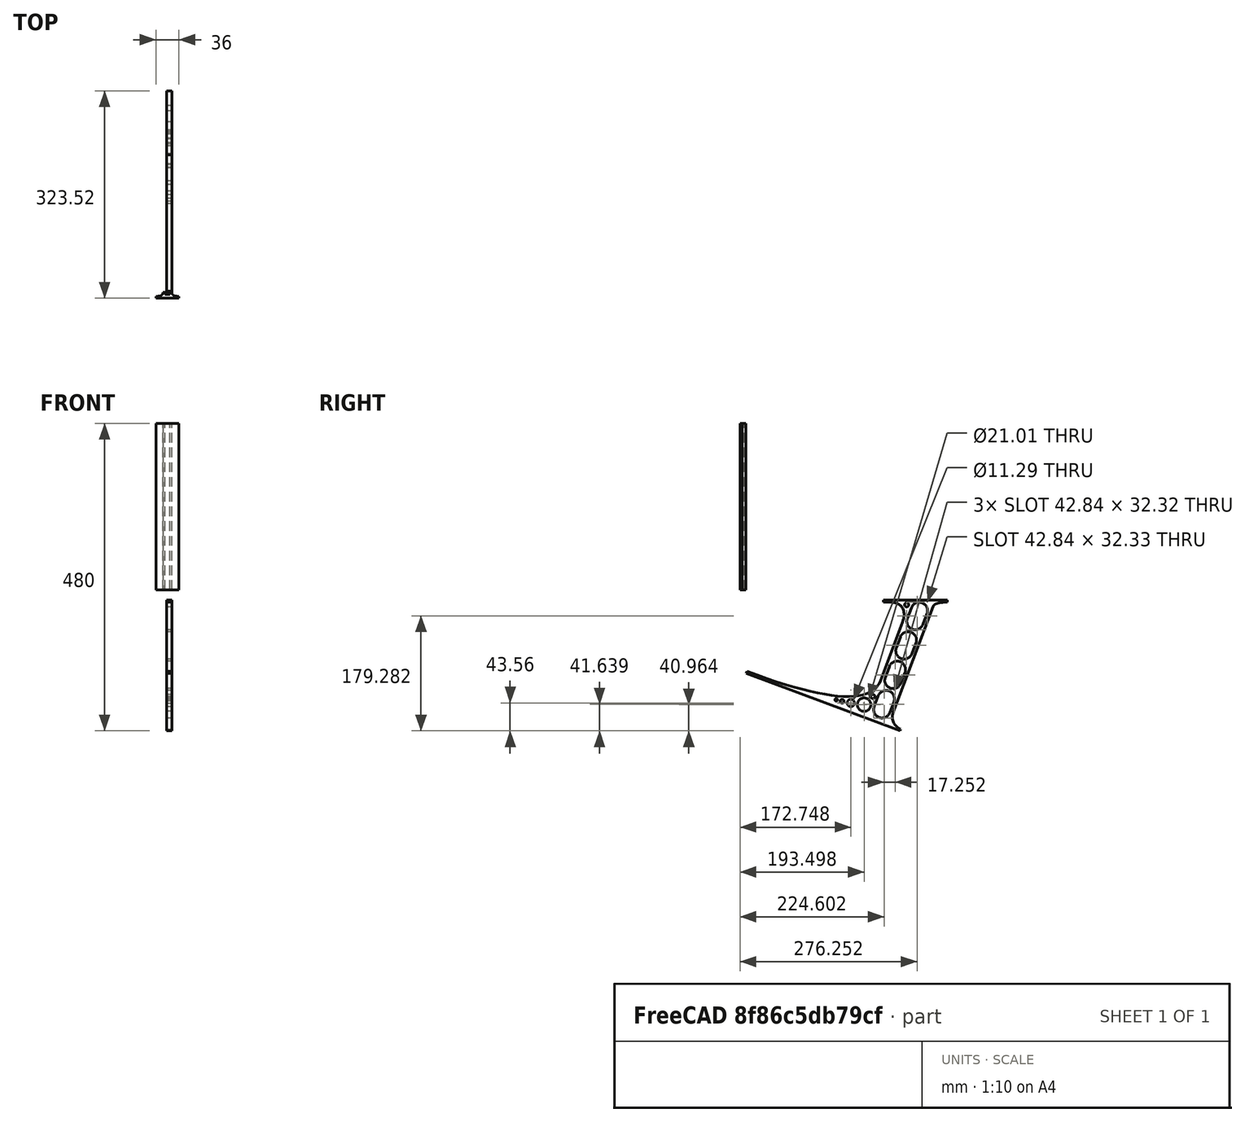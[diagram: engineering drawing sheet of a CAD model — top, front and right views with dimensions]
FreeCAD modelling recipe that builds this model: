
FCSTD DOCUMENT  (FreeCAD 0.19R0.19.2)
Label: laptopStand116FCStd
License: All rights reserved
LicenseURL: http://en.wikipedia.org/wiki/All_rights_reserved
objects: Sketcher::SketchObject×3, Part::Extrusion×3
note: 6 computed .brp shape members not serialized (recipe doc carries the construction recipe); baked Part::Feature solids carry a one-line shape summary decoded from their .brp

FEATURE [Sketcher::SketchObject] Sketch
  FullyConstrained = true
  sketch-geometry (342):
    g0: LineSegment StartX=-10.9272 StartY=-82.7794 StartZ=0 EndX=46.0728 EndY=-51.4823 EndZ=0
    g1: LineSegment StartX=-10.9272 StartY=77.3346 StartZ=0 EndX=-10.9272 EndY=-82.7794 EndZ=0
    g2: LineSegment StartX=-1.92719 StartY=-91.7794 StartZ=0 EndX=46.0728 EndY=-91.7794 EndZ=0
    g3: LineSegment StartX=46.0728 StartY=-65.424 StartZ=0 EndX=-1.92719 EndY=-91.7794 EndZ=0
    g4: LineSegment StartX=46.0728 StartY=-65.424 StartZ=0 EndX=46.0728 EndY=-91.7794 EndZ=0
    g5: LineSegment StartX=46.0728 StartY=77.3346 StartZ=0 EndX=46.0728 EndY=-51.4823 EndZ=0
    g6: LineSegment StartX=-42.9272 StartY=136.221 StartZ=0 EndX=-42.9272 EndY=-103.779 EndZ=0
    g7: LineSegment StartX=407.073 StartY=136.221 StartZ=0 EndX=407.073 EndY=-103.779 EndZ=0
    g8: ArcOfCircle CenterX=-26.9272 CenterY=22.1087 CenterZ=0 NormalX=0 NormalY=0 NormalZ=1 AngleXU=0 Radius=8 StartAngle=1e-16 EndAngle=3.14159
    g9: ArcOfCircle CenterX=-26.9272 CenterY=-83.7794 CenterZ=0 NormalX=0 NormalY=0 NormalZ=1 AngleXU=0 Radius=8 StartAngle=3.14159 EndAngle=6.28319
    g10: LineSegment StartX=-34.9272 StartY=22.1087 StartZ=0 EndX=-34.9272 EndY=-83.7794 EndZ=0
    g11: LineSegment StartX=-18.9272 StartY=22.1087 StartZ=0 EndX=-18.9272 EndY=-83.7794 EndZ=0
    g12: ArcOfCircle CenterX=391.073 CenterY=22.1087 CenterZ=0 NormalX=0 NormalY=0 NormalZ=1 AngleXU=0 Radius=8 StartAngle=-4.4e-15 EndAngle=3.14159
    g13: LineSegment StartX=399.073 StartY=22.1087 StartZ=0 EndX=399.073 EndY=-83.7794 EndZ=0
    g14: LineSegment StartX=383.073 StartY=22.1087 StartZ=0 EndX=383.073 EndY=-83.7794 EndZ=0
    g15: ArcOfCircle CenterX=391.073 CenterY=-83.7794 CenterZ=0 NormalX=0 NormalY=0 NormalZ=1 AngleXU=0 Radius=8 StartAngle=3.14159 EndAngle=6.28319
    g16: Circle CenterX=175.022 CenterY=27.0628 CenterZ=0 NormalX=0 NormalY=0 NormalZ=1 AngleXU=0 Radius=1
    g17: Circle CenterX=179.022 CenterY=24.8665 CenterZ=0 NormalX=0 NormalY=0 NormalZ=1 AngleXU=0 Radius=1
    g18: Circle CenterX=179.022 CenterY=27.0628 CenterZ=0 NormalX=0 NormalY=0 NormalZ=1 AngleXU=0 Radius=1
    g19: BSplineCurve PolesCount=3 KnotsCount=2 Degree=2 IsPeriodic=0
    g20: GeomPoint X=175.022 Y=27.0628 Z=0
    g21: GeomPoint X=179.022 Y=27.0628 Z=0
    g22: Circle CenterX=189.124 CenterY=27.0628 CenterZ=0 NormalX=0 NormalY=0 NormalZ=1 AngleXU=0 Radius=1
    g23: Circle CenterX=185.124 CenterY=24.8665 CenterZ=0 NormalX=0 NormalY=0 NormalZ=1 AngleXU=0 Radius=1
    g24: Circle CenterX=185.124 CenterY=27.0628 CenterZ=0 NormalX=0 NormalY=0 NormalZ=1 AngleXU=0 Radius=1
    g25: BSplineCurve PolesCount=3 KnotsCount=2 Degree=2 IsPeriodic=0
    g26: GeomPoint X=189.124 Y=27.0628 Z=0
    g27: GeomPoint X=185.124 Y=27.0628 Z=0
    g28: Circle CenterX=175.022 CenterY=5.37834 CenterZ=0 NormalX=0 NormalY=0 NormalZ=1 AngleXU=0 Radius=1
    g29: Circle CenterX=179.022 CenterY=7.57463 CenterZ=0 NormalX=0 NormalY=0 NormalZ=1 AngleXU=0 Radius=1
    g30: Circle CenterX=179.022 CenterY=5.34704 CenterZ=0 NormalX=0 NormalY=0 NormalZ=1 AngleXU=0 Radius=1
    g31: BSplineCurve PolesCount=3 KnotsCount=2 Degree=2 IsPeriodic=0
    g32: GeomPoint X=175.022 Y=5.37834 Z=0
    g33: GeomPoint X=179.022 Y=5.34704 Z=0
    g34: Circle CenterX=189.124 CenterY=5.37834 CenterZ=0 NormalX=0 NormalY=0 NormalZ=1 AngleXU=0 Radius=1
    g35: Circle CenterX=185.124 CenterY=7.57463 CenterZ=0 NormalX=0 NormalY=0 NormalZ=1 AngleXU=0 Radius=1
    g36: Circle CenterX=185.124 CenterY=5.34704 CenterZ=0 NormalX=0 NormalY=0 NormalZ=1 AngleXU=0 Radius=1
    g37: BSplineCurve PolesCount=3 KnotsCount=2 Degree=2 IsPeriodic=0
    g38: GeomPoint X=189.124 Y=5.37834 Z=0
    g39: GeomPoint X=185.124 Y=5.34704 Z=0
    g40: Circle CenterX=165.871 CenterY=18.1458 CenterZ=0 NormalX=0 NormalY=0 NormalZ=1 AngleXU=0 Radius=1
    g41: Circle CenterX=169.377 CenterY=16.2206 CenterZ=0 NormalX=0 NormalY=0 NormalZ=1 AngleXU=0 Radius=1
    g42: Circle CenterX=165.871 CenterY=14.2954 CenterZ=0 NormalX=0 NormalY=0 NormalZ=1 AngleXU=0 Radius=1
    g43: BSplineCurve PolesCount=3 KnotsCount=2 Degree=2 IsPeriodic=0
    g44: GeomPoint X=165.871 Y=18.1458 Z=0
    g45: GeomPoint X=165.871 Y=14.2954 Z=0
    g46: Circle CenterX=198.275 CenterY=18.1458 CenterZ=0 NormalX=0 NormalY=0 NormalZ=1 AngleXU=0 Radius=1
    g47: Circle CenterX=194.768 CenterY=16.2206 CenterZ=0 NormalX=0 NormalY=0 NormalZ=1 AngleXU=0 Radius=1
    g48: Circle CenterX=198.275 CenterY=14.2954 CenterZ=0 NormalX=0 NormalY=0 NormalZ=1 AngleXU=0 Radius=1
    g49: BSplineCurve PolesCount=3 KnotsCount=2 Degree=2 IsPeriodic=0
    g50: GeomPoint X=198.275 Y=18.1458 Z=0
    g51: GeomPoint X=198.275 Y=14.2954 Z=0
    g52: LineSegment StartX=407.073 StartY=-103.779 StartZ=0 EndX=-42.9272 EndY=-103.779 EndZ=0
    g53: LineSegment StartX=407.073 StartY=136.221 StartZ=0 EndX=-42.9272 EndY=136.221 EndZ=0
    g54: LineSegment StartX=46.0728 StartY=77.3346 StartZ=0 EndX=-10.9272 EndY=77.3346 EndZ=0
    g55: LineSegment StartX=46.0728 StartY=105.865 StartZ=0 EndX=31.5028 EndY=105.865 EndZ=0
    g56: LineSegment StartX=46.0728 StartY=124.221 StartZ=0 EndX=46.0728 EndY=105.865 EndZ=0
    g57: LineSegment StartX=-1.92719 StartY=124.221 StartZ=0 EndX=31.5028 EndY=105.865 EndZ=0
    g58: LineSegment StartX=46.0728 StartY=124.221 StartZ=0 EndX=-1.92719 EndY=124.221 EndZ=0
    g59: Circle CenterX=125.607 CenterY=54.1951 CenterZ=0 NormalX=0 NormalY=0 NormalZ=1 AngleXU=0 Radius=1
    g60: Circle CenterX=139.632 CenterY=46.4944 CenterZ=0 NormalX=0 NormalY=0 NormalZ=1 AngleXU=0 Radius=1
    g61: Circle CenterX=127.326 CenterY=56.7187 CenterZ=0 NormalX=0 NormalY=0 NormalZ=1 AngleXU=0 Radius=1
    g62: BSplineCurve PolesCount=3 KnotsCount=2 Degree=2 IsPeriodic=0
    g63: GeomPoint X=125.607 Y=54.1951 Z=0
    g64: GeomPoint X=127.326 Y=56.7187 Z=0
    g65: Circle CenterX=236.821 CenterY=56.7187 CenterZ=0 NormalX=0 NormalY=0 NormalZ=1 AngleXU=0 Radius=1
    g66: Circle CenterX=224.513 CenterY=46.4944 CenterZ=0 NormalX=0 NormalY=0 NormalZ=1 AngleXU=0 Radius=1
    g67: Circle CenterX=238.538 CenterY=54.1951 CenterZ=0 NormalX=0 NormalY=0 NormalZ=1 AngleXU=0 Radius=1
    g68: BSplineCurve PolesCount=3 KnotsCount=2 Degree=2 IsPeriodic=0
    g69: GeomPoint X=236.821 Y=56.7187 Z=0
    g70: GeomPoint X=238.538 Y=54.1951 Z=0
    g71: Circle CenterX=238.538 CenterY=-21.7539 CenterZ=0 NormalX=0 NormalY=0 NormalZ=1 AngleXU=0 Radius=1
    g72: Circle CenterX=224.513 CenterY=-14.0532 CenterZ=0 NormalX=0 NormalY=0 NormalZ=1 AngleXU=0 Radius=1
    g73: Circle CenterX=236.821 CenterY=-24.2775 CenterZ=0 NormalX=0 NormalY=0 NormalZ=1 AngleXU=0 Radius=1
    g74: BSplineCurve PolesCount=3 KnotsCount=2 Degree=2 IsPeriodic=0
    g75: GeomPoint X=238.538 Y=-21.7539 Z=0
    g76: GeomPoint X=236.821 Y=-24.2775 Z=0
    g77: Circle CenterX=125.607 CenterY=-21.7539 CenterZ=0 NormalX=0 NormalY=0 NormalZ=1 AngleXU=0 Radius=1
    g78: Circle CenterX=139.632 CenterY=-14.0532 CenterZ=0 NormalX=0 NormalY=0 NormalZ=1 AngleXU=0 Radius=1
    g79: Circle CenterX=127.325 CenterY=-24.2775 CenterZ=0 NormalX=0 NormalY=0 NormalZ=1 AngleXU=0 Radius=1
    g80: BSplineCurve PolesCount=3 KnotsCount=2 Degree=2 IsPeriodic=0
    g81: GeomPoint X=125.607 Y=-21.7539 Z=0
    g82: GeomPoint X=127.325 Y=-24.2775 Z=0
    g83: Circle CenterX=302.996 CenterY=111.695 CenterZ=0 NormalX=0 NormalY=0 NormalZ=1 AngleXU=0 Radius=1
    g84: Circle CenterX=306.073 CenterY=114.251 CenterZ=0 NormalX=0 NormalY=0 NormalZ=1 AngleXU=0 Radius=1
    g85: Circle CenterX=306.073 CenterY=110.251 CenterZ=0 NormalX=0 NormalY=0 NormalZ=1 AngleXU=0 Radius=1
    g86: BSplineCurve PolesCount=3 KnotsCount=2 Degree=2 IsPeriodic=0
    g87: GeomPoint X=302.996 Y=111.695 Z=0
    g88: GeomPoint X=306.073 Y=110.251 Z=0
    g89: Circle CenterX=306.073 CenterY=95.2763 CenterZ=0 NormalX=0 NormalY=0 NormalZ=1 AngleXU=0 Radius=1
    g90: Circle CenterX=306.073 CenterY=91.2763 CenterZ=0 NormalX=0 NormalY=0 NormalZ=1 AngleXU=0 Radius=1
    g91: Circle CenterX=302.567 CenterY=89.3511 CenterZ=0 NormalX=0 NormalY=0 NormalZ=1 AngleXU=0 Radius=1
    g92: BSplineCurve PolesCount=3 KnotsCount=2 Degree=2 IsPeriodic=0
    g93: GeomPoint X=306.073 Y=95.2763 Z=0
    g94: GeomPoint X=302.567 Y=89.3511 Z=0
    g95: LineSegment StartX=306.073 StartY=110.251 StartZ=0 EndX=306.073 EndY=95.2763 EndZ=0
    g96: LineSegment StartX=302.996 StartY=111.695 StartZ=0 EndX=236.821 EndY=56.7187 EndZ=0
    g97: LineSegment StartX=238.538 StartY=54.1951 StartZ=0 EndX=302.567 EndY=89.3511 EndZ=0
    g98: Circle CenterX=61.1496 CenterY=111.695 CenterZ=0 NormalX=0 NormalY=0 NormalZ=1 AngleXU=0 Radius=1
    g99: Circle CenterX=58.0728 CenterY=114.251 CenterZ=0 NormalX=0 NormalY=0 NormalZ=1 AngleXU=0 Radius=1
    g100: Circle CenterX=58.0728 CenterY=110.251 CenterZ=0 NormalX=0 NormalY=0 NormalZ=1 AngleXU=0 Radius=1
    g101: BSplineCurve PolesCount=3 KnotsCount=2 Degree=2 IsPeriodic=0
    g102: GeomPoint X=61.1496 Y=111.695 Z=0
    g103: GeomPoint X=58.0728 Y=110.251 Z=0
    g104: Circle CenterX=61.5791 CenterY=89.3511 CenterZ=0 NormalX=0 NormalY=0 NormalZ=1 AngleXU=0 Radius=1
    g105: Circle CenterX=58.0728 CenterY=91.2763 CenterZ=0 NormalX=0 NormalY=0 NormalZ=1 AngleXU=0 Radius=1
    g106: Circle CenterX=58.0728 CenterY=95.2763 CenterZ=0 NormalX=0 NormalY=0 NormalZ=1 AngleXU=0 Radius=1
    g107: BSplineCurve PolesCount=3 KnotsCount=2 Degree=2 IsPeriodic=0
    g108: GeomPoint X=61.5791 Y=89.3511 Z=0
    g109: GeomPoint X=58.0728 Y=95.2763 Z=0
    g110: LineSegment StartX=58.0728 StartY=110.251 StartZ=0 EndX=58.0728 EndY=95.2763 EndZ=0
    g111: LineSegment StartX=61.1496 StartY=111.695 StartZ=0 EndX=127.326 EndY=56.7187 EndZ=0
    g112: LineSegment StartX=125.607 StartY=54.1951 StartZ=0 EndX=61.5791 EndY=89.3511 EndZ=0
    g113: Circle CenterX=61.5791 CenterY=-56.9099 CenterZ=0 NormalX=0 NormalY=0 NormalZ=1 AngleXU=0 Radius=1
    g114: Circle CenterX=58.0728 CenterY=-58.8351 CenterZ=0 NormalX=0 NormalY=0 NormalZ=1 AngleXU=0 Radius=1
    g115: Circle CenterX=58.0728 CenterY=-62.8351 CenterZ=0 NormalX=0 NormalY=0 NormalZ=1 AngleXU=0 Radius=1
    g116: BSplineCurve PolesCount=3 KnotsCount=2 Degree=2 IsPeriodic=0
    g117: GeomPoint X=61.5791 Y=-56.9099 Z=0
    g118: GeomPoint X=58.0728 Y=-62.8351 Z=0
    g119: Circle CenterX=58.0728 CenterY=-77.8102 CenterZ=0 NormalX=0 NormalY=0 NormalZ=1 AngleXU=0 Radius=1
    g120: Circle CenterX=58.0728 CenterY=-81.8102 CenterZ=0 NormalX=0 NormalY=0 NormalZ=1 AngleXU=0 Radius=1
    g121: Circle CenterX=61.1496 CenterY=-79.2541 CenterZ=0 NormalX=0 NormalY=0 NormalZ=1 AngleXU=0 Radius=1
    g122: BSplineCurve PolesCount=3 KnotsCount=2 Degree=2 IsPeriodic=0
    g123: GeomPoint X=58.0728 Y=-77.8102 Z=0
    g124: GeomPoint X=61.1496 Y=-79.2541 Z=0
    g125: LineSegment StartX=58.0728 StartY=-62.8351 StartZ=0 EndX=58.0728 EndY=-77.8102 EndZ=0
    g126: LineSegment StartX=61.1496 StartY=-79.2541 StartZ=0 EndX=127.325 EndY=-24.2775 EndZ=0
    g127: LineSegment StartX=125.607 StartY=-21.7539 StartZ=0 EndX=61.5791 EndY=-56.9099 EndZ=0
    g128: Circle CenterX=302.567 CenterY=-56.9099 CenterZ=0 NormalX=0 NormalY=0 NormalZ=1 AngleXU=0 Radius=1
    g129: Circle CenterX=306.073 CenterY=-58.8351 CenterZ=0 NormalX=0 NormalY=0 NormalZ=1 AngleXU=0 Radius=1
    g130: Circle CenterX=306.073 CenterY=-62.8351 CenterZ=0 NormalX=0 NormalY=0 NormalZ=1 AngleXU=0 Radius=1
    g131: BSplineCurve PolesCount=3 KnotsCount=2 Degree=2 IsPeriodic=0
    g132: GeomPoint X=302.567 Y=-56.9099 Z=0
    g133: GeomPoint X=306.073 Y=-62.8351 Z=0
    g134: Circle CenterX=302.996 CenterY=-79.2541 CenterZ=0 NormalX=0 NormalY=0 NormalZ=1 AngleXU=0 Radius=1
    g135: Circle CenterX=306.073 CenterY=-81.8102 CenterZ=0 NormalX=0 NormalY=0 NormalZ=1 AngleXU=0 Radius=1
    g136: Circle CenterX=306.073 CenterY=-77.8102 CenterZ=0 NormalX=0 NormalY=0 NormalZ=1 AngleXU=0 Radius=1
    g137: BSplineCurve PolesCount=3 KnotsCount=2 Degree=2 IsPeriodic=0
    g138: GeomPoint X=302.996 Y=-79.2541 Z=0
    g139: GeomPoint X=306.073 Y=-77.8102 Z=0
    g140: LineSegment StartX=306.073 StartY=-62.8351 StartZ=0 EndX=306.073 EndY=-77.8102 EndZ=0
    g141: LineSegment StartX=302.996 StartY=-79.2541 StartZ=0 EndX=236.821 EndY=-24.2775 EndZ=0
    g142: LineSegment StartX=238.538 StartY=-21.7539 StartZ=0 EndX=302.567 EndY=-56.9099 EndZ=0
    g143: Circle CenterX=61.6457 CenterY=-88.8112 CenterZ=0 NormalX=0 NormalY=0 NormalZ=1 AngleXU=0 Radius=1
    g144: Circle CenterX=58.0728 CenterY=-91.7794 CenterZ=0 NormalX=0 NormalY=0 NormalZ=1 AngleXU=0 Radius=1
    g145: Circle CenterX=63.9135 CenterY=-91.7794 CenterZ=0 NormalX=0 NormalY=0 NormalZ=1 AngleXU=0 Radius=1
    g146: BSplineCurve PolesCount=3 KnotsCount=2 Degree=2 IsPeriodic=0
    g147: GeomPoint X=61.6457 Y=-88.8112 Z=0
    g148: GeomPoint X=63.9135 Y=-91.7794 Z=0
    g149: Circle CenterX=179.022 CenterY=-85.8163 CenterZ=0 NormalX=0 NormalY=0 NormalZ=1 AngleXU=0 Radius=1
    g150: Circle CenterX=179.022 CenterY=-91.7794 CenterZ=0 NormalX=0 NormalY=0 NormalZ=1 AngleXU=0 Radius=1
    g151: Circle CenterX=171.895 CenterY=-91.7794 CenterZ=0 NormalX=0 NormalY=0 NormalZ=1 AngleXU=0 Radius=1
    g152: BSplineCurve PolesCount=3 KnotsCount=2 Degree=2 IsPeriodic=0
    g153: GeomPoint X=179.022 Y=-85.8163 Z=0
    g154: GeomPoint X=171.895 Y=-91.7794 Z=0
    g155: Circle CenterX=185.124 CenterY=-86.2028 CenterZ=0 NormalX=0 NormalY=0 NormalZ=1 AngleXU=0 Radius=1
    g156: Circle CenterX=185.124 CenterY=-91.7794 CenterZ=0 NormalX=0 NormalY=0 NormalZ=1 AngleXU=0 Radius=1
    g157: Circle CenterX=191.747 CenterY=-91.7794 CenterZ=0 NormalX=0 NormalY=0 NormalZ=1 AngleXU=0 Radius=1
    g158: BSplineCurve PolesCount=3 KnotsCount=2 Degree=2 IsPeriodic=0
    g159: GeomPoint X=185.124 Y=-86.2028 Z=0
    g160: GeomPoint X=191.747 Y=-91.7794 Z=0
    g161: Circle CenterX=299.888 CenterY=-86.6413 CenterZ=0 NormalX=0 NormalY=0 NormalZ=1 AngleXU=0 Radius=1
    g162: Circle CenterX=306.073 CenterY=-91.7794 CenterZ=0 NormalX=0 NormalY=0 NormalZ=1 AngleXU=0 Radius=1
    g163: Circle CenterX=298.776 CenterY=-91.7794 CenterZ=0 NormalX=0 NormalY=0 NormalZ=1 AngleXU=0 Radius=1
    g164: BSplineCurve PolesCount=3 KnotsCount=2 Degree=2 IsPeriodic=0
    g165: GeomPoint X=299.888 Y=-86.6413 Z=0
    g166: GeomPoint X=298.776 Y=-91.7794 Z=0
    g167: LineSegment StartX=189.124 StartY=5.37834 StartZ=0 EndX=299.888 EndY=-86.6413 EndZ=0
    g168: LineSegment StartX=298.776 StartY=-91.7794 StartZ=0 EndX=191.747 EndY=-91.7794 EndZ=0
    g169: LineSegment StartX=185.124 StartY=-86.2028 StartZ=0 EndX=185.124 EndY=5.34704 EndZ=0
    g170: LineSegment StartX=179.022 StartY=5.34704 StartZ=0 EndX=179.022 EndY=-85.8163 EndZ=0
    g171: LineSegment StartX=171.895 StartY=-91.7794 StartZ=0 EndX=63.9135 EndY=-91.7794 EndZ=0
    g172: LineSegment StartX=61.6457 StartY=-88.8112 StartZ=0 EndX=175.022 EndY=5.37834 EndZ=0
    g173: Circle CenterX=302.073 CenterY=124.221 CenterZ=0 NormalX=0 NormalY=0 NormalZ=1 AngleXU=0 Radius=1
    g174: Circle CenterX=306.073 CenterY=124.221 CenterZ=0 NormalX=0 NormalY=0 NormalZ=1 AngleXU=0 Radius=1
    g175: Circle CenterX=302.996 CenterY=121.665 CenterZ=0 NormalX=0 NormalY=0 NormalZ=1 AngleXU=0 Radius=1
    g176: BSplineCurve PolesCount=3 KnotsCount=2 Degree=2 IsPeriodic=0
    g177: GeomPoint X=302.073 Y=124.221 Z=0
    g178: GeomPoint X=302.996 Y=121.665 Z=0
    g179: Circle CenterX=189.124 CenterY=124.221 CenterZ=0 NormalX=0 NormalY=0 NormalZ=1 AngleXU=0 Radius=1
    g180: Circle CenterX=185.124 CenterY=124.221 CenterZ=0 NormalX=0 NormalY=0 NormalZ=1 AngleXU=0 Radius=1
    g181: Circle CenterX=185.124 CenterY=120.221 CenterZ=0 NormalX=0 NormalY=0 NormalZ=1 AngleXU=0 Radius=1
    g182: BSplineCurve PolesCount=3 KnotsCount=2 Degree=2 IsPeriodic=0
    g183: GeomPoint X=189.124 Y=124.221 Z=0
    g184: GeomPoint X=185.124 Y=120.221 Z=0
    g185: Circle CenterX=175.022 CenterY=124.221 CenterZ=0 NormalX=0 NormalY=0 NormalZ=1 AngleXU=0 Radius=1
    g186: Circle CenterX=179.022 CenterY=124.221 CenterZ=0 NormalX=0 NormalY=0 NormalZ=1 AngleXU=0 Radius=1
    g187: Circle CenterX=179.022 CenterY=120.221 CenterZ=0 NormalX=0 NormalY=0 NormalZ=1 AngleXU=0 Radius=1
    g188: BSplineCurve PolesCount=3 KnotsCount=2 Degree=2 IsPeriodic=0
    g189: GeomPoint X=175.022 Y=124.221 Z=0
    g190: GeomPoint X=179.022 Y=120.221 Z=0
    g191: Circle CenterX=62.0728 CenterY=124.221 CenterZ=0 NormalX=0 NormalY=0 NormalZ=1 AngleXU=0 Radius=1
    g192: Circle CenterX=58.0728 CenterY=124.221 CenterZ=0 NormalX=0 NormalY=0 NormalZ=1 AngleXU=0 Radius=1
    g193: Circle CenterX=61.1496 CenterY=121.665 CenterZ=0 NormalX=0 NormalY=0 NormalZ=1 AngleXU=0 Radius=1
    g194: BSplineCurve PolesCount=3 KnotsCount=2 Degree=2 IsPeriodic=0
    g195: GeomPoint X=62.0728 Y=124.221 Z=0
    g196: GeomPoint X=61.1496 Y=121.665 Z=0
    g197: LineSegment StartX=62.0728 StartY=124.221 StartZ=0 EndX=175.022 EndY=124.221 EndZ=0
    g198: LineSegment StartX=179.022 StartY=120.221 StartZ=0 EndX=179.022 EndY=27.0628 EndZ=0
    g199: LineSegment StartX=185.124 StartY=27.0628 StartZ=0 EndX=185.124 EndY=120.221 EndZ=0
    g200: LineSegment StartX=189.124 StartY=124.221 StartZ=0 EndX=302.073 EndY=124.221 EndZ=0
    g201: LineSegment StartX=302.996 StartY=121.665 StartZ=0 EndX=189.124 EndY=27.0628 EndZ=0
    g202: LineSegment StartX=175.022 StartY=27.0628 StartZ=0 EndX=61.1496 EndY=121.665 EndZ=0
    g203: Circle CenterX=61.5791 CenterY=75.4095 CenterZ=0 NormalX=0 NormalY=0 NormalZ=1 AngleXU=0 Radius=1
    g204: Circle CenterX=58.0728 CenterY=77.3346 CenterZ=0 NormalX=0 NormalY=0 NormalZ=1 AngleXU=0 Radius=1
    g205: Circle CenterX=58.0728 CenterY=73.3346 CenterZ=0 NormalX=0 NormalY=0 NormalZ=1 AngleXU=0 Radius=1
    g206: BSplineCurve PolesCount=3 KnotsCount=2 Degree=2 IsPeriodic=0
    g207: GeomPoint X=61.5791 Y=75.4095 Z=0
    g208: GeomPoint X=58.0728 Y=73.3346 Z=0
    g209: Circle CenterX=58.0728 CenterY=-40.8935 CenterZ=0 NormalX=0 NormalY=0 NormalZ=1 AngleXU=0 Radius=1
    g210: Circle CenterX=58.0728 CenterY=-44.8935 CenterZ=0 NormalX=0 NormalY=0 NormalZ=1 AngleXU=0 Radius=1
    g211: Circle CenterX=61.5791 CenterY=-42.9683 CenterZ=0 NormalX=0 NormalY=0 NormalZ=1 AngleXU=0 Radius=1
    g212: BSplineCurve PolesCount=3 KnotsCount=2 Degree=2 IsPeriodic=0
    g213: GeomPoint X=58.0728 Y=-40.8935 Z=0
    g214: GeomPoint X=61.5791 Y=-42.9683 Z=0
    g215: LineSegment StartX=61.5791 StartY=-42.9683 StartZ=0 EndX=165.871 EndY=14.2954 EndZ=0
    g216: LineSegment StartX=165.871 StartY=18.1458 StartZ=0 EndX=61.5791 EndY=75.4095 EndZ=0
    g217: LineSegment StartX=58.0728 StartY=73.3346 StartZ=0 EndX=58.0728 EndY=-40.8935 EndZ=0
    g218: Circle CenterX=302.567 CenterY=-42.9683 CenterZ=0 NormalX=0 NormalY=0 NormalZ=1 AngleXU=0 Radius=1
    g219: Circle CenterX=306.073 CenterY=-44.8935 CenterZ=0 NormalX=0 NormalY=0 NormalZ=1 AngleXU=0 Radius=1
    g220: Circle CenterX=306.073 CenterY=-40.8935 CenterZ=0 NormalX=0 NormalY=0 NormalZ=1 AngleXU=0 Radius=1
    g221: BSplineCurve PolesCount=3 KnotsCount=2 Degree=2 IsPeriodic=0
    g222: GeomPoint X=302.567 Y=-42.9683 Z=0
    g223: GeomPoint X=306.073 Y=-40.8935 Z=0
    g224: Circle CenterX=306.073 CenterY=73.3346 CenterZ=0 NormalX=0 NormalY=0 NormalZ=1 AngleXU=0 Radius=1
    g225: Circle CenterX=306.073 CenterY=77.3346 CenterZ=0 NormalX=0 NormalY=0 NormalZ=1 AngleXU=0 Radius=1
    g226: Circle CenterX=302.567 CenterY=75.4095 CenterZ=0 NormalX=0 NormalY=0 NormalZ=1 AngleXU=0 Radius=1
    g227: BSplineCurve PolesCount=3 KnotsCount=2 Degree=2 IsPeriodic=0
    g228: GeomPoint X=306.073 Y=73.3346 Z=0
    g229: GeomPoint X=302.567 Y=75.4095 Z=0
    g230: LineSegment StartX=302.567 StartY=-42.9683 StartZ=0 EndX=198.275 EndY=14.2954 EndZ=0
    g231: LineSegment StartX=198.275 StartY=18.1458 StartZ=0 EndX=302.567 EndY=75.4095 EndZ=0
    g232: LineSegment StartX=306.073 StartY=73.3346 StartZ=0 EndX=306.073 EndY=-40.8935 EndZ=0
    g233: LineSegment StartX=322.073 StartY=105.865 StartZ=0 EndX=328.643 EndY=105.865 EndZ=0
    g234: LineSegment StartX=318.073 StartY=120.221 StartZ=0 EndX=318.073 EndY=109.865 EndZ=0
    g235: LineSegment StartX=336.157 StartY=107.779 StartZ=0 EndX=362.567 EndY=122.294 EndZ=0
    g236: Circle CenterX=362.073 CenterY=124.221 CenterZ=0 NormalX=0 NormalY=0 NormalZ=1 AngleXU=0 Radius=1
    g237: Circle CenterX=366.073 CenterY=124.221 CenterZ=0 NormalX=0 NormalY=0 NormalZ=1 AngleXU=0 Radius=1
    g238: Circle CenterX=362.567 CenterY=122.294 CenterZ=0 NormalX=0 NormalY=0 NormalZ=1 AngleXU=0 Radius=1
    g239: BSplineCurve PolesCount=3 KnotsCount=2 Degree=2 IsPeriodic=0
    g240: GeomPoint X=362.073 Y=124.221 Z=0
    g241: GeomPoint X=362.567 Y=122.294 Z=0
    g242: Circle CenterX=322.073 CenterY=124.221 CenterZ=0 NormalX=0 NormalY=0 NormalZ=1 AngleXU=0 Radius=1
    g243: Circle CenterX=318.073 CenterY=124.221 CenterZ=0 NormalX=0 NormalY=0 NormalZ=1 AngleXU=0 Radius=1
    g244: Circle CenterX=318.073 CenterY=120.221 CenterZ=0 NormalX=0 NormalY=0 NormalZ=1 AngleXU=0 Radius=1
    g245: BSplineCurve PolesCount=3 KnotsCount=2 Degree=2 IsPeriodic=0
    g246: GeomPoint X=322.073 Y=124.221 Z=0
    g247: GeomPoint X=318.073 Y=120.221 Z=0
    g248: Circle CenterX=322.073 CenterY=105.865 CenterZ=0 NormalX=0 NormalY=0 NormalZ=1 AngleXU=0 Radius=1
    g249: Circle CenterX=318.073 CenterY=105.865 CenterZ=0 NormalX=0 NormalY=0 NormalZ=1 AngleXU=0 Radius=1
    g250: Circle CenterX=318.073 CenterY=109.865 CenterZ=0 NormalX=0 NormalY=0 NormalZ=1 AngleXU=0 Radius=1
    g251: BSplineCurve PolesCount=3 KnotsCount=2 Degree=2 IsPeriodic=0
    g252: GeomPoint X=322.073 Y=105.865 Z=0
    g253: GeomPoint X=318.073 Y=109.865 Z=0
    g254: Circle CenterX=336.157 CenterY=107.779 CenterZ=0 NormalX=0 NormalY=0 NormalZ=1 AngleXU=0 Radius=1
    g255: Circle CenterX=332.651 CenterY=105.853 CenterZ=0 NormalX=0 NormalY=0 NormalZ=1 AngleXU=0 Radius=1
    g256: Circle CenterX=328.643 CenterY=105.865 CenterZ=0 NormalX=0 NormalY=0 NormalZ=1 AngleXU=0 Radius=1
    g257: BSplineCurve PolesCount=3 KnotsCount=2 Degree=2 IsPeriodic=0
    g258: GeomPoint X=336.157 Y=107.779 Z=0
    g259: GeomPoint X=328.643 Y=105.865 Z=0
    g260: LineSegment StartX=322.073 StartY=124.221 StartZ=0 EndX=362.073 EndY=124.221 EndZ=0
    g261: Circle CenterX=371.567 CenterY=-80.8644 CenterZ=0 NormalX=0 NormalY=0 NormalZ=1 AngleXU=0 Radius=1
    g262: Circle CenterX=375.073 CenterY=-82.7896 CenterZ=0 NormalX=0 NormalY=0 NormalZ=1 AngleXU=0 Radius=1
    g263: Circle CenterX=375.073 CenterY=-78.7896 CenterZ=0 NormalX=0 NormalY=0 NormalZ=1 AngleXU=0 Radius=1
    g264: BSplineCurve PolesCount=3 KnotsCount=2 Degree=2 IsPeriodic=0
    g265: GeomPoint X=371.567 Y=-80.8644 Z=0
    g266: GeomPoint X=375.073 Y=-78.7896 Z=0
    g267: Circle CenterX=321.579 CenterY=-53.4075 CenterZ=0 NormalX=0 NormalY=0 NormalZ=1 AngleXU=0 Radius=1
    g268: Circle CenterX=318.073 CenterY=-51.4823 CenterZ=0 NormalX=0 NormalY=0 NormalZ=1 AngleXU=0 Radius=1
    g269: Circle CenterX=318.073 CenterY=-47.4823 CenterZ=0 NormalX=0 NormalY=0 NormalZ=1 AngleXU=0 Radius=1
    g270: BSplineCurve PolesCount=3 KnotsCount=2 Degree=2 IsPeriodic=0
    g271: GeomPoint X=321.579 Y=-53.4075 Z=0
    g272: GeomPoint X=318.073 Y=-47.4823 Z=0
    g273: Circle CenterX=318.073 CenterY=79.9235 CenterZ=0 NormalX=0 NormalY=0 NormalZ=1 AngleXU=0 Radius=1
    g274: Circle CenterX=318.073 CenterY=83.9235 CenterZ=0 NormalX=0 NormalY=0 NormalZ=1 AngleXU=0 Radius=1
    g275: Circle CenterX=322.073 CenterY=83.9235 CenterZ=0 NormalX=0 NormalY=0 NormalZ=1 AngleXU=0 Radius=1
    g276: BSplineCurve PolesCount=3 KnotsCount=2 Degree=2 IsPeriodic=0
    g277: GeomPoint X=318.073 Y=79.9235 Z=0
    g278: GeomPoint X=322.073 Y=83.9235 Z=0
    g279: Circle CenterX=375.073 CenterY=79.9235 CenterZ=0 NormalX=0 NormalY=0 NormalZ=1 AngleXU=0 Radius=1
    g280: Circle CenterX=375.073 CenterY=83.9235 CenterZ=0 NormalX=0 NormalY=0 NormalZ=1 AngleXU=0 Radius=1
    g281: Circle CenterX=371.073 CenterY=83.9235 CenterZ=0 NormalX=0 NormalY=0 NormalZ=1 AngleXU=0 Radius=1
    g282: BSplineCurve PolesCount=3 KnotsCount=2 Degree=2 IsPeriodic=0
    g283: GeomPoint X=375.073 Y=79.9235 Z=0
    g284: GeomPoint X=371.073 Y=83.9235 Z=0
    g285: LineSegment StartX=322.073 StartY=83.9235 StartZ=0 EndX=371.073 EndY=83.9235 EndZ=0
    g286: LineSegment StartX=375.073 StartY=79.9235 StartZ=0 EndX=375.073 EndY=-78.7896 EndZ=0
    g287: LineSegment StartX=371.567 StartY=-80.8644 StartZ=0 EndX=321.579 EndY=-53.4075 EndZ=0
    g288: LineSegment StartX=318.073 StartY=-47.4823 StartZ=0 EndX=318.073 EndY=79.9235 EndZ=0
    g289: Circle CenterX=321.579 CenterY=-67.3492 CenterZ=0 NormalX=0 NormalY=0 NormalZ=1 AngleXU=0 Radius=1
    g290: Circle CenterX=318.073 CenterY=-65.424 CenterZ=0 NormalX=0 NormalY=0 NormalZ=1 AngleXU=0 Radius=1
    g291: Circle CenterX=318.073 CenterY=-69.424 CenterZ=0 NormalX=0 NormalY=0 NormalZ=1 AngleXU=0 Radius=1
    g292: BSplineCurve PolesCount=3 KnotsCount=2 Degree=2 IsPeriodic=0
    g293: GeomPoint X=321.579 Y=-67.3492 Z=0
    g294: GeomPoint X=318.073 Y=-69.424 Z=0
    g295: Circle CenterX=362.567 CenterY=-89.8542 CenterZ=0 NormalX=0 NormalY=0 NormalZ=1 AngleXU=0 Radius=1
    g296: Circle CenterX=366.073 CenterY=-91.7794 CenterZ=0 NormalX=0 NormalY=0 NormalZ=1 AngleXU=0 Radius=1
    g297: Circle CenterX=362.073 CenterY=-91.7794 CenterZ=0 NormalX=0 NormalY=0 NormalZ=1 AngleXU=0 Radius=1
    g298: BSplineCurve PolesCount=3 KnotsCount=2 Degree=2 IsPeriodic=0
    g299: GeomPoint X=362.567 Y=-89.8542 Z=0
    g300: GeomPoint X=362.073 Y=-91.7794 Z=0
    g301: Circle CenterX=322.073 CenterY=-91.7794 CenterZ=0 NormalX=0 NormalY=0 NormalZ=1 AngleXU=0 Radius=1
    g302: Circle CenterX=318.073 CenterY=-91.7794 CenterZ=0 NormalX=0 NormalY=0 NormalZ=1 AngleXU=0 Radius=1
    g303: Circle CenterX=318.073 CenterY=-87.7794 CenterZ=0 NormalX=0 NormalY=0 NormalZ=1 AngleXU=0 Radius=1
    g304: BSplineCurve PolesCount=3 KnotsCount=2 Degree=2 IsPeriodic=0
    g305: GeomPoint X=322.073 Y=-91.7794 Z=0
    g306: GeomPoint X=318.073 Y=-87.7794 Z=0
    g307: LineSegment StartX=362.567 StartY=-89.8542 StartZ=0 EndX=321.579 EndY=-67.3492 EndZ=0
    g308: LineSegment StartX=318.073 StartY=-69.424 StartZ=0 EndX=318.073 EndY=-87.7794 EndZ=0
    g309: LineSegment StartX=322.073 StartY=-91.7794 StartZ=0 EndX=362.073 EndY=-91.7794 EndZ=0
    g310: LineSegment StartX=-1.92719 StartY=124.221 StartZ=0 EndX=2.07281 EndY=124.221 EndZ=0
    g311: LineSegment StartX=-1.92719 StartY=124.221 StartZ=0 EndX=1.57905 EndY=122.295 EndZ=0
    g312: LineSegment StartX=31.5028 StartY=105.865 StartZ=0 EndX=27.9965 EndY=107.79 EndZ=0
    g313: LineSegment StartX=31.5028 StartY=105.865 StartZ=0 EndX=35.5028 EndY=105.865 EndZ=0
    g314: LineSegment StartX=46.0728 StartY=105.865 StartZ=0 EndX=42.0728 EndY=105.865 EndZ=0
    g315: LineSegment StartX=46.0728 StartY=105.865 StartZ=0 EndX=46.0728 EndY=109.865 EndZ=0
    g316: LineSegment StartX=46.0728 StartY=124.221 StartZ=0 EndX=46.0728 EndY=120.221 EndZ=0
    g317: LineSegment StartX=46.0728 StartY=124.221 StartZ=0 EndX=42.0728 EndY=124.221 EndZ=0
    g318: Circle CenterX=2.07281 CenterY=124.221 CenterZ=0 NormalX=0 NormalY=0 NormalZ=1 AngleXU=0 Radius=1
    g319: Circle CenterX=-1.92719 CenterY=124.221 CenterZ=0 NormalX=0 NormalY=0 NormalZ=1 AngleXU=0 Radius=1
    g320: Circle CenterX=1.57905 CenterY=122.295 CenterZ=0 NormalX=0 NormalY=0 NormalZ=1 AngleXU=0 Radius=1
    g321: BSplineCurve PolesCount=3 KnotsCount=2 Degree=2 IsPeriodic=0
    g322: GeomPoint X=2.07281 Y=124.221 Z=0
    g323: GeomPoint X=1.57905 Y=122.295 Z=0
    g324: Circle CenterX=42.0728 CenterY=124.221 CenterZ=0 NormalX=0 NormalY=0 NormalZ=1 AngleXU=0 Radius=1
    g325: Circle CenterX=46.0728 CenterY=124.221 CenterZ=0 NormalX=0 NormalY=0 NormalZ=1 AngleXU=0 Radius=1
    g326: Circle CenterX=46.0728 CenterY=120.221 CenterZ=0 NormalX=0 NormalY=0 NormalZ=1 AngleXU=0 Radius=1
    g327: BSplineCurve PolesCount=3 KnotsCount=2 Degree=2 IsPeriodic=0
    g328: GeomPoint X=42.0728 Y=124.221 Z=0
    g329: GeomPoint X=46.0728 Y=120.221 Z=0
    g330: Circle CenterX=46.0728 CenterY=109.865 CenterZ=0 NormalX=0 NormalY=0 NormalZ=1 AngleXU=0 Radius=1
    g331: Circle CenterX=46.0728 CenterY=105.865 CenterZ=0 NormalX=0 NormalY=0 NormalZ=1 AngleXU=0 Radius=1
    g332: Circle CenterX=42.0728 CenterY=105.865 CenterZ=0 NormalX=0 NormalY=0 NormalZ=1 AngleXU=0 Radius=1
    g333: BSplineCurve PolesCount=3 KnotsCount=2 Degree=2 IsPeriodic=0
    g334: GeomPoint X=46.0728 Y=109.865 Z=0
    g335: GeomPoint X=42.0728 Y=105.865 Z=0
    g336: Circle CenterX=35.5028 CenterY=105.865 CenterZ=0 NormalX=0 NormalY=0 NormalZ=1 AngleXU=0 Radius=1
    g337: Circle CenterX=31.5028 CenterY=105.865 CenterZ=0 NormalX=0 NormalY=0 NormalZ=1 AngleXU=0 Radius=1
    g338: Circle CenterX=27.9965 CenterY=107.79 CenterZ=0 NormalX=0 NormalY=0 NormalZ=1 AngleXU=0 Radius=1
    g339: BSplineCurve PolesCount=3 KnotsCount=2 Degree=2 IsPeriodic=0
    g340: GeomPoint X=35.5028 Y=105.865 Z=0
    g341: GeomPoint X=27.9965 Y=107.79 Z=0
  constraints (587):
    c: Horizontal(g2)
    c: Coincident(g4,g3)
    c: Coincident(g0,g5)
    c: Block(g4)
    c: Block(g3)
    c: Block(g0)
    c: Block(g1)
    c: Block(g2)
    c: Vertical(g6)
    c: Vertical(g7)
    c: Block(g7)
    c: Block(g6)
    c: Tangent(g8,g11) = 1.5708
    c: Tangent(g8,g10) = -1.5708
    c: Tangent(g10,g9) = -1.5708
    c: Tangent(g11,g9) = 1.5708
    c: Vertical(g10)
    c: Equal(g8,g9)
    c: Block(g11)
    c: Block(g10)
    c: Tangent(g12,g13) = 1.5708
    c: Tangent(g13,g15) = 1.5708
    c: Equal(g12,g15)
    c: Coincident(g14,g12)
    c: Coincident(g14,g15)
    c: Block(g13)
    c: Block(g14)
    c: Weight(g16) = 1
    c: Equal(g16,g17)
    c: Equal(g16,g18)
    c: InternalAlignment(g16,g19)
    c: InternalAlignment(g17,g19)
    c: InternalAlignment(g18,g19)
    c: InternalAlignment(g20,g19)
    c: InternalAlignment(g21,g19)
    c: Weight(g22) = 1
    c: Equal(g22,g23)
    c: Equal(g22,g24)
    c: InternalAlignment(g22,g25)
    c: InternalAlignment(g23,g25)
    c: InternalAlignment(g24,g25)
    c: InternalAlignment(g26,g25)
    c: InternalAlignment(g27,g25)
    c: Block(g25)
    c: Block(g19)
    c: Weight(g28) = 1
    c: Equal(g28,g29)
    c: Equal(g28,g30)
    c: InternalAlignment(g28,g31)
    c: InternalAlignment(g29,g31)
    c: InternalAlignment(g30,g31)
    c: InternalAlignment(g32,g31)
    c: InternalAlignment(g33,g31)
    c: Weight(g34) = 1
    c: Equal(g34,g35)
    c: Equal(g34,g36)
    c: InternalAlignment(g34,g37)
    c: InternalAlignment(g35,g37)
    c: InternalAlignment(g36,g37)
    c: InternalAlignment(g38,g37)
    c: InternalAlignment(g39,g37)
    c: Block(g37)
    c: Block(g31)
    c: Weight(g40) = 1
    c: Equal(g40,g41)
    c: Equal(g40,g42)
    c: InternalAlignment(g40,g43)
    c: InternalAlignment(g41,g43)
    c: InternalAlignment(g42,g43)
    c: InternalAlignment(g44,g43)
    c: InternalAlignment(g45,g43)
    c: Weight(g46) = 1
    c: Equal(g46,g47)
    c: Equal(g46,g48)
    c: InternalAlignment(g46,g49)
    c: InternalAlignment(g47,g49)
    c: InternalAlignment(g48,g49)
    c: InternalAlignment(g50,g49)
    c: InternalAlignment(g51,g49)
    c: Block(g43)
    c: Block(g49)
    c: Coincident(g52,g7)
    c: Coincident(g52,g6)
    c: Horizontal(g52)
    c: Distance(g52) = 450
    c: Coincident(g53,g7)
    c: Coincident(g53,g6)
    c: Horizontal(g53)
    c: Horizontal(g54)
    c: Coincident(g5,g54)
    c: Horizontal(g55)
    c: Vertical(g56)
    c: Block(g56)
    c: Block(g55)
    c: Block(g54)
    c: Distance(g56) = 18.3554
    c: Coincident(g58,g56)
    c: Coincident(g58,g57)
    c: Horizontal(g58)
    c: Block(g58)
    c: Block(g57)
    c: Coincident(g55,g57)
    c: Coincident(g1,g54)
    c: Weight(g59) = 1
    c: Equal(g59,g60)
    c: Equal(g59,g61)
    c: InternalAlignment(g59,g62)
    c: InternalAlignment(g60,g62)
    c: InternalAlignment(g61,g62)
    c: InternalAlignment(g63,g62)
    c: InternalAlignment(g64,g62)
    c: Block(g62)
    c: Weight(g65) = 1
    c: Equal(g65,g66)
    c: Equal(g65,g67)
    c: InternalAlignment(g65,g68)
    c: InternalAlignment(g66,g68)
    c: InternalAlignment(g67,g68)
    c: InternalAlignment(g69,g68)
    c: InternalAlignment(g70,g68)
    c: Block(g68)
    c: Weight(g71) = 1
    c: Equal(g71,g72)
    c: Equal(g71,g73)
    c: InternalAlignment(g71,g74)
    c: InternalAlignment(g72,g74)
    c: InternalAlignment(g73,g74)
    c: InternalAlignment(g75,g74)
    c: InternalAlignment(g76,g74)
    c: Block(g74)
    c: Weight(g77) = 1
    c: Equal(g77,g78)
    c: Equal(g77,g79)
    c: InternalAlignment(g77,g80)
    c: InternalAlignment(g78,g80)
    c: InternalAlignment(g79,g80)
    c: InternalAlignment(g81,g80)
    c: InternalAlignment(g82,g80)
    c: Block(g80)
    c: Weight(g83) = 1
    c: Equal(g83,g84)
    c: Equal(g83,g85)
    c: InternalAlignment(g83,g86)
    c: InternalAlignment(g84,g86)
    c: InternalAlignment(g85,g86)
    c: InternalAlignment(g87,g86)
    c: InternalAlignment(g88,g86)
    c: Weight(g89) = 1
    c: Equal(g89,g90)
    c: Equal(g89,g91)
    c: InternalAlignment(g89,g92)
    c: InternalAlignment(g90,g92)
    c: InternalAlignment(g91,g92)
    c: InternalAlignment(g93,g92)
    c: InternalAlignment(g94,g92)
    c: Block(g86)
    c: Block(g92)
    c: Coincident(g95,g86)
    c: Coincident(g95,g92)
    c: Vertical(g95)
    c: Coincident(g96,g86)
    c: Coincident(g96,g68)
    c: Coincident(g97,g68)
    c: Coincident(g97,g92)
    c: Weight(g98) = 1
    c: Equal(g98,g99)
    c: Equal(g98,g100)
    c: InternalAlignment(g98,g101)
    c: InternalAlignment(g99,g101)
    c: InternalAlignment(g100,g101)
    c: InternalAlignment(g102,g101)
    c: InternalAlignment(g103,g101)
    c: Weight(g104) = 1
    c: Equal(g104,g105)
    c: Equal(g104,g106)
    c: InternalAlignment(g104,g107)
    c: InternalAlignment(g105,g107)
    c: InternalAlignment(g106,g107)
    c: InternalAlignment(g108,g107)
    c: InternalAlignment(g109,g107)
    c: Block(g101)
    c: Block(g107)
    c: Coincident(g110,g101)
    c: Coincident(g110,g107)
    c: Vertical(g110)
    c: Coincident(g111,g101)
    c: Coincident(g111,g62)
    c: Coincident(g112,g62)
    c: Coincident(g112,g107)
    c: Weight(g113) = 1
    c: Equal(g113,g114)
    c: Equal(g113,g115)
    c: InternalAlignment(g113,g116)
    c: InternalAlignment(g114,g116)
    c: InternalAlignment(g115,g116)
    c: InternalAlignment(g117,g116)
    c: InternalAlignment(g118,g116)
    c: Weight(g119) = 1
    c: Equal(g119,g120)
    c: Equal(g119,g121)
    c: InternalAlignment(g119,g122)
    c: InternalAlignment(g120,g122)
    c: InternalAlignment(g121,g122)
    c: InternalAlignment(g123,g122)
    c: InternalAlignment(g124,g122)
    c: Block(g116)
    c: Block(g122)
    c: Coincident(g125,g116)
    c: Coincident(g125,g122)
    c: Vertical(g125)
    c: Coincident(g126,g122)
    c: Coincident(g126,g80)
    c: Coincident(g127,g80)
    c: Coincident(g127,g116)
    c: Weight(g128) = 1
    c: Equal(g128,g129)
    c: Equal(g128,g130)
    c: InternalAlignment(g128,g131)
    c: InternalAlignment(g129,g131)
    c: InternalAlignment(g130,g131)
    c: InternalAlignment(g132,g131)
    c: InternalAlignment(g133,g131)
    c: Weight(g134) = 1
    c: Equal(g134,g135)
    c: Equal(g134,g136)
    c: InternalAlignment(g134,g137)
    c: InternalAlignment(g135,g137)
    c: InternalAlignment(g136,g137)
    c: InternalAlignment(g138,g137)
    c: InternalAlignment(g139,g137)
    c: Block(g131)
    c: Block(g137)
    c: Coincident(g140,g131)
    c: Coincident(g140,g137)
    c: Vertical(g140)
    c: Coincident(g141,g137)
    c: Coincident(g141,g74)
    c: Coincident(g142,g74)
    c: Coincident(g142,g131)
    c: Weight(g143) = 1
    c: Equal(g143,g144)
    c: Equal(g143,g145)
    c: InternalAlignment(g143,g146)
    c: InternalAlignment(g144,g146)
    c: InternalAlignment(g145,g146)
    c: InternalAlignment(g147,g146)
    c: InternalAlignment(g148,g146)
    c: Weight(g149) = 1
    c: Equal(g149,g150)
    c: Equal(g149,g151)
    c: InternalAlignment(g149,g152)
    c: InternalAlignment(g150,g152)
    c: InternalAlignment(g151,g152)
    c: InternalAlignment(g153,g152)
    c: InternalAlignment(g154,g152)
    c: Weight(g155) = 1
    c: Equal(g155,g156)
    c: Equal(g155,g157)
    c: InternalAlignment(g155,g158)
    c: InternalAlignment(g156,g158)
    c: InternalAlignment(g157,g158)
    c: InternalAlignment(g159,g158)
    c: InternalAlignment(g160,g158)
    c: Weight(g161) = 1
    c: Equal(g161,g162)
    c: Equal(g161,g163)
    c: InternalAlignment(g161,g164)
    c: InternalAlignment(g162,g164)
    c: InternalAlignment(g163,g164)
    c: InternalAlignment(g165,g164)
    c: InternalAlignment(g166,g164)
    c: Block(g164)
    c: Block(g158)
    c: Block(g152)
    c: Block(g146)
    c: Coincident(g167,g37)
    c: Coincident(g167,g164)
    c: Coincident(g168,g164)
    c: Coincident(g168,g158)
    c: Horizontal(g168)
    c: Coincident(g169,g158)
    c: Coincident(g169,g37)
    c: Vertical(g169)
    c: Coincident(g170,g31)
    c: Coincident(g170,g152)
    c: Vertical(g170)
    c: Coincident(g171,g152)
    c: Coincident(g171,g146)
    c: Horizontal(g171)
    c: Coincident(g172,g146)
    c: Coincident(g172,g31)
    c: Weight(g173) = 1
    c: Equal(g173,g174)
    c: Equal(g173,g175)
    c: InternalAlignment(g173,g176)
    c: InternalAlignment(g174,g176)
    c: InternalAlignment(g175,g176)
    c: InternalAlignment(g177,g176)
    c: InternalAlignment(g178,g176)
    c: Weight(g179) = 1
    c: Equal(g179,g180)
    c: Equal(g179,g181)
    c: InternalAlignment(g179,g182)
    c: InternalAlignment(g180,g182)
    c: InternalAlignment(g181,g182)
    c: InternalAlignment(g183,g182)
    c: InternalAlignment(g184,g182)
    c: Weight(g185) = 1
    c: Equal(g185,g186)
    c: Equal(g185,g187)
    c: InternalAlignment(g185,g188)
    c: InternalAlignment(g186,g188)
    c: InternalAlignment(g187,g188)
    c: InternalAlignment(g189,g188)
    c: InternalAlignment(g190,g188)
    c: Weight(g191) = 1
    c: Equal(g191,g192)
    c: Equal(g191,g193)
    c: InternalAlignment(g191,g194)
    c: InternalAlignment(g192,g194)
    c: InternalAlignment(g193,g194)
    c: InternalAlignment(g195,g194)
    c: InternalAlignment(g196,g194)
    c: Block(g194)
    c: Block(g188)
    c: Block(g182)
    c: Block(g176)
    c: Coincident(g197,g194)
    c: Coincident(g197,g188)
    c: Horizontal(g197)
    c: Coincident(g198,g188)
    c: Coincident(g198,g19)
    c: Vertical(g198)
    c: Coincident(g199,g25)
    c: Coincident(g199,g182)
    c: Vertical(g199)
    c: Coincident(g200,g182)
    c: Coincident(g200,g176)
    c: Horizontal(g200)
    c: Coincident(g201,g176)
    c: Coincident(g201,g25)
    c: Coincident(g202,g19)
    c: Weight(g203) = 1
    c: Equal(g203,g204)
    c: Equal(g203,g205)
    c: InternalAlignment(g203,g206)
    c: InternalAlignment(g204,g206)
    c: InternalAlignment(g205,g206)
    c: InternalAlignment(g207,g206)
    c: InternalAlignment(g208,g206)
    c: Weight(g209) = 1
    c: Equal(g209,g210)
    c: Equal(g209,g211)
    c: InternalAlignment(g209,g212)
    c: InternalAlignment(g210,g212)
    c: InternalAlignment(g211,g212)
    c: InternalAlignment(g213,g212)
    c: InternalAlignment(g214,g212)
    c: Block(g212)
    c: Block(g206)
    c: Coincident(g215,g212)
    c: Coincident(g215,g43)
    c: Coincident(g216,g43)
    c: Coincident(g216,g206)
    c: Coincident(g217,g206)
    c: Coincident(g217,g212)
    c: Vertical(g217)
    c: Weight(g218) = 1
    c: Equal(g218,g219)
    c: Equal(g218,g220)
    c: InternalAlignment(g218,g221)
    c: InternalAlignment(g219,g221)
    c: InternalAlignment(g220,g221)
    c: InternalAlignment(g222,g221)
    c: InternalAlignment(g223,g221)
    c: Weight(g224) = 1
    c: Equal(g224,g225)
    c: Equal(g224,g226)
    c: InternalAlignment(g224,g227)
    c: InternalAlignment(g225,g227)
    c: InternalAlignment(g226,g227)
    c: InternalAlignment(g228,g227)
    c: InternalAlignment(g229,g227)
    c: Block(g227)
    c: Block(g221)
    c: Coincident(g230,g221)
    c: Coincident(g230,g49)
    c: Coincident(g231,g49)
    c: Coincident(g231,g227)
    c: Coincident(g232,g227)
    c: Coincident(g232,g221)
    c: Vertical(g232)
    c: Horizontal(g233)
    c: Block(g233)
    c: Vertical(g234)
    c: Block(g234)
    c: Block(g235)
    c: Weight(g236) = 1
    c: Equal(g236,g237)
    c: Equal(g236,g238)
    c: InternalAlignment(g236,g239)
    c: InternalAlignment(g237,g239)
    c: InternalAlignment(g238,g239)
    c: InternalAlignment(g240,g239)
    c: InternalAlignment(g241,g239)
    c: Weight(g242) = 1
    c: Equal(g242,g243)
    c: Equal(g242,g244)
    c: InternalAlignment(g242,g245)
    c: InternalAlignment(g243,g245)
    c: InternalAlignment(g244,g245)
    c: InternalAlignment(g246,g245)
    c: InternalAlignment(g247,g245)
    c: Weight(g248) = 1
    c: Equal(g248,g249)
    c: Equal(g248,g250)
    c: InternalAlignment(g248,g251)
    c: InternalAlignment(g249,g251)
    c: InternalAlignment(g250,g251)
    c: InternalAlignment(g252,g251)
    c: InternalAlignment(g253,g251)
    c: Weight(g254) = 1
    c: Equal(g254,g255)
    c: Equal(g254,g256)
    c: InternalAlignment(g254,g257)
    c: InternalAlignment(g255,g257)
    c: InternalAlignment(g256,g257)
    c: InternalAlignment(g258,g257)
    c: InternalAlignment(g259,g257)
    c: Block(g239)
    c: Block(g245)
    c: Block(g251)
    c: Block(g257)
    c: Coincident(g260,g245)
    c: Coincident(g260,g239)
    c: Horizontal(g260)
    c: Block(g202)
    c: Weight(g261) = 1
    c: Equal(g261,g262)
    c: Equal(g261,g263)
    c: InternalAlignment(g261,g264)
    c: InternalAlignment(g262,g264)
    c: InternalAlignment(g263,g264)
    c: InternalAlignment(g265,g264)
    c: InternalAlignment(g266,g264)
    c: Weight(g267) = 1
    c: Equal(g267,g268)
    c: Equal(g267,g269)
    c: InternalAlignment(g267,g270)
    c: InternalAlignment(g268,g270)
    c: InternalAlignment(g269,g270)
    c: InternalAlignment(g271,g270)
    c: InternalAlignment(g272,g270)
    c: Weight(g273) = 1
    c: Equal(g273,g274)
    c: Equal(g273,g275)
    c: InternalAlignment(g273,g276)
    c: InternalAlignment(g274,g276)
    c: InternalAlignment(g275,g276)
    c: InternalAlignment(g277,g276)
    c: InternalAlignment(g278,g276)
    c: Weight(g279) = 1
    c: Equal(g279,g280)
    c: Equal(g279,g281)
    c: InternalAlignment(g279,g282)
    c: InternalAlignment(g280,g282)
    c: InternalAlignment(g281,g282)
    c: InternalAlignment(g283,g282)
    c: InternalAlignment(g284,g282)
    c: Block(g264)
    c: Block(g270)
    c: Block(g276)
    c: Block(g282)
    c: Coincident(g285,g276)
    c: Coincident(g285,g282)
    c: Horizontal(g285)
    c: Coincident(g286,g282)
    c: Coincident(g286,g264)
    c: Vertical(g286)
    c: Coincident(g287,g264)
    c: Coincident(g287,g270)
    c: Coincident(g288,g270)
    c: Coincident(g288,g276)
    c: Vertical(g288)
    c: Weight(g289) = 1
    c: Equal(g289,g290)
    c: Equal(g289,g291)
    c: InternalAlignment(g289,g292)
    c: InternalAlignment(g290,g292)
    c: InternalAlignment(g291,g292)
    c: InternalAlignment(g293,g292)
    c: InternalAlignment(g294,g292)
    c: Weight(g295) = 1
    c: Equal(g295,g296)
    c: Equal(g295,g297)
    c: InternalAlignment(g295,g298)
    c: InternalAlignment(g296,g298)
    c: InternalAlignment(g297,g298)
    c: InternalAlignment(g299,g298)
    c: InternalAlignment(g300,g298)
    c: Weight(g301) = 1
    c: Equal(g301,g302)
    c: Equal(g301,g303)
    c: InternalAlignment(g301,g304)
    c: InternalAlignment(g302,g304)
    c: InternalAlignment(g303,g304)
    c: InternalAlignment(g305,g304)
    c: InternalAlignment(g306,g304)
    c: Block(g304)
    c: Block(g298)
    c: Block(g292)
    c: Coincident(g307,g298)
    c: Coincident(g307,g292)
    c: Coincident(g308,g292)
    c: Coincident(g308,g304)
    c: Vertical(g308)
    c: Coincident(g309,g304)
    c: Coincident(g309,g298)
    c: Horizontal(g309)
    c: Horizontal(g310)
    c: Horizontal(g313)
    c: Horizontal(g314)
    c: Vertical(g315)
    c: Vertical(g316)
    c: Horizontal(g317)
    c: Distance(g316) = 4
    c: Distance(g317) = 4
    c: Distance(g315) = 4
    c: Distance(g314) = 4
    c: Distance(g313) = 4
    c: Distance(g312) = 4
    c: Distance(g311) = 4
    c: Distance(g310) = 4
    c: Parallel(g57,g311)
    c: Parallel(g57,g312)
    c: Coincident(g312,g55)
    c: Coincident(g313,g55)
    c: Coincident(g314,g315)
    c: Coincident(g314,g55)
    c: Coincident(g316,g317)
    c: Coincident(g56,g316)
    c: Coincident(g310,g311)
    c: Coincident(g310,g57)
    c: Coincident(g321,g310)
    c: Weight(g318) = 1
    c: Equal(g318,g319)
    c: Coincident(g319,g57)
    c: Equal(g318,g320)
    c: Coincident(g321,g311)
    c: InternalAlignment(g318,g321)
    c: InternalAlignment(g319,g321)
    c: InternalAlignment(g320,g321)
    c: InternalAlignment(g322,g321)
    c: InternalAlignment(g323,g321)
    c: Coincident(g327,g317)
    c: Weight(g324) = 1
    c: Equal(g324,g325)
    c: Coincident(g325,g56)
    c: Equal(g324,g326)
    c: Coincident(g327,g316)
    c: InternalAlignment(g324,g327)
    c: InternalAlignment(g325,g327)
    c: InternalAlignment(g326,g327)
    c: InternalAlignment(g328,g327)
    c: InternalAlignment(g329,g327)
    c: Coincident(g333,g315)
    c: Weight(g330) = 1
    c: Equal(g330,g331)
    c: Coincident(g331,g55)
    c: Equal(g330,g332)
    c: Coincident(g333,g314)
    c: InternalAlignment(g330,g333)
    c: InternalAlignment(g331,g333)
    c: InternalAlignment(g332,g333)
    c: InternalAlignment(g334,g333)
    c: InternalAlignment(g335,g333)
    c: Coincident(g339,g313)
    c: Weight(g336) = 1
    c: Equal(g336,g337)
    c: Coincident(g337,g55)
    c: Equal(g336,g338)
    c: Coincident(g339,g312)
    c: InternalAlignment(g336,g339)
    c: InternalAlignment(g337,g339)
    c: InternalAlignment(g338,g339)
    c: InternalAlignment(g340,g339)
    c: InternalAlignment(g341,g339)
FEATURE [Sketcher::SketchObject] Sketch001
  FullyConstrained = true
  MapMode = 4
  Placement = pos=(0,0,0) rot=(0.57735,0.57735,0.57735;2.0944rad)
  Support = -> [Sketch]
  sketch-geometry (46):
    g0: BSplineCurve PolesCount=3 KnotsCount=2 Degree=2 IsPeriodic=0
    g1: ArcOfCircle CenterX=73.1223 CenterY=-32.291 CenterZ=0 NormalX=0 NormalY=0 NormalZ=1 AngleXU=0 Radius=13 StartAngle=5.92268 EndAngle=9.06428
    g2: ArcOfCircle CenterX=66.7816 CenterY=-49.1439 CenterZ=0 NormalX=0 NormalY=0 NormalZ=1 AngleXU=0 Radius=13 StartAngle=2.78068 EndAngle=5.92131
    g3: ArcOfCircle CenterX=55.9263 CenterY=-78.1807 CenterZ=0 NormalX=0 NormalY=0 NormalZ=1 AngleXU=0 Radius=13 StartAngle=5.92268 EndAngle=9.06428
    g4: ArcOfCircle CenterX=49.5884 CenterY=-95.0342 CenterZ=0 NormalX=0 NormalY=0 NormalZ=1 AngleXU=0 Radius=13 StartAngle=2.78068 EndAngle=5.92131
    g5: ArcOfCircle CenterX=38.7206 CenterY=-124.067 CenterZ=0 NormalX=0 NormalY=0 NormalZ=1 AngleXU=0 Radius=13 StartAngle=5.92268 EndAngle=9.06428
    g6: ArcOfCircle CenterX=32.3875 CenterY=-140.92 CenterZ=0 NormalX=0 NormalY=0 NormalZ=1 AngleXU=0 Radius=13 StartAngle=2.78068 EndAngle=5.92131
    g7: ArcOfCircle CenterX=21.4715 CenterY=-169.934 CenterZ=0 NormalX=0 NormalY=0 NormalZ=1 AngleXU=0 Radius=13 StartAngle=5.92268 EndAngle=9.06428
    g8: ArcOfCircle CenterX=15.1336 CenterY=-186.787 CenterZ=0 NormalX=0 NormalY=0 NormalZ=1 AngleXU=0 Radius=13 StartAngle=2.78068 EndAngle=5.92131
    g9-g12: Circle x4 (B-spline internal-alignment scaffolding for g13; pole/knot coordinates omitted)
    g13: BSplineCurve PolesCount=4 KnotsCount=2 Degree=3 IsPeriodic=0
    g14: GeomPoint X=28.8094 Y=-19.0875 Z=0
    g15: GeomPoint X=47.0443 Y=-50.4712 Z=0
    g16: Circle CenterX=53.5586 CenterY=-23.2695 CenterZ=0 NormalX=0 NormalY=0 NormalZ=1 AngleXU=0 Radius=3.24518
    g17: Circle CenterX=-195.441 CenterY=-127.082 CenterZ=0 NormalX=0 NormalY=0 NormalZ=1 AngleXU=0 Radius=1
    g18: Circle CenterX=-8.24091 CenterY=-197.481 CenterZ=0 NormalX=0 NormalY=0 NormalZ=1 AngleXU=0 Radius=1
    g19: Circle CenterX=12.8789 CenterY=-141.321 CenterZ=0 NormalX=0 NormalY=0 NormalZ=1 AngleXU=0 Radius=1
    g20: BSplineCurve PolesCount=3 KnotsCount=2 Degree=2 IsPeriodic=0
    g21: GeomPoint X=-195.441 Y=-127.082 Z=0
    g22: GeomPoint X=12.8789 Y=-141.321 Z=0
    g23: Circle CenterX=-12.8016 CenterY=-179.036 CenterZ=0 NormalX=0 NormalY=0 NormalZ=1 AngleXU=0 Radius=10.5072
    g24: Circle CenterX=0.933922 CenterY=-166.43 CenterZ=0 NormalX=0 NormalY=0 NormalZ=1 AngleXU=0 Radius=3.26661
    g25: Circle CenterX=-33.5518 CenterY=-176.44 CenterZ=0 NormalX=0 NormalY=0 NormalZ=1 AngleXU=0 Radius=5.64388
    g26: Circle CenterX=-47.2366 CenterY=-173.859 CenterZ=0 NormalX=0 NormalY=0 NormalZ=1 AngleXU=0 Radius=3.01653
    g27: Circle CenterX=-56.2595 CenterY=-171.456 CenterZ=0 NormalX=0 NormalY=0 NormalZ=1 AngleXU=0 Radius=2.12826
    g28: ArcOfCircle CenterX=51.2151 CenterY=-198.473 CenterZ=0 NormalX=0 NormalY=0 NormalZ=1 AngleXU=0 Radius=20 StartAngle=2.78189 EndAngle=4.35269
    g29: LineSegment StartX=32.4951 StartY=-191.433 StartZ=0 EndX=94.6578 EndY=-26.1352 EndZ=0
    g30: LineSegment StartX=43.1192 StartY=-220.001 StartZ=0 EndX=-196.497 EndY=-129.89 EndZ=0
    g31: LineSegment StartX=43.1192 StartY=-220.001 StartZ=0 EndX=44.1752 EndY=-217.193 EndZ=0
    g32: LineSegment StartX=117.223 StartY=-19.0875 StartZ=0 EndX=117.223 EndY=-16.0875 EndZ=0
    g33: LineSegment StartX=117.223 StartY=-16.0875 StartZ=0 EndX=17.2232 EndY=-16.0875 EndZ=0
    g34: LineSegment StartX=17.2232 StartY=-16.0875 StartZ=0 EndX=17.2232 EndY=-19.0875 EndZ=0
    g35: LineSegment StartX=28.8094 StartY=-19.0875 StartZ=0 EndX=17.2232 EndY=-19.0875 EndZ=0
    g36: LineSegment StartX=47.0443 StartY=-50.4712 StartZ=0 EndX=12.8789 EndY=-141.321 EndZ=0
    g37: LineSegment StartX=-195.441 StartY=-127.082 StartZ=0 EndX=-196.497 EndY=-129.89 EndZ=0
    g38: LineSegment StartX=85.2866 StartY=-36.8766 StartZ=0 EndX=78.9396 EndY=-53.7463 EndZ=0
    g39: LineSegment StartX=60.9579 StartY=-27.7053 StartZ=0 EndX=54.6191 EndY=-44.5532 EndZ=0
    g40: LineSegment StartX=68.0907 StartY=-82.7664 StartZ=0 EndX=61.7465 EndY=-99.6365 EndZ=0
    g41: LineSegment StartX=43.7619 StartY=-73.595 StartZ=0 EndX=37.426 EndY=-90.4435 EndZ=0
    g42: LineSegment StartX=50.885 StartY=-128.652 StartZ=0 EndX=44.5456 EndY=-145.522 EndZ=0
    g43: LineSegment StartX=26.5562 StartY=-119.481 StartZ=0 EndX=20.2251 EndY=-136.329 EndZ=0
    g44: LineSegment StartX=9.3071 StartY=-165.349 StartZ=0 EndX=2.97115 EndY=-182.197 EndZ=0
    g45: LineSegment StartX=33.6358 StartY=-174.52 StartZ=0 EndX=27.2917 EndY=-191.39 EndZ=0
  constraints (71):
    c: Block(g0)
    c: Block(g1)
    c: Block(g2)
    c: Block(g4)
    c: Block(g3)
    c: Block(g6)
    c: Block(g5)
    c: Block(g8)
    c: Block(g7)
    c: Weight(g9) = 1
    c: Equal(g9,g10)
    c: Equal(g9,g11)
    c: Equal(g9,g12)
    c: InternalAlignment(g9-g12 -> g13) x4
    c: InternalAlignment(g14,g13)
    c: InternalAlignment(g15,g13)
    c: Block(g16)
    c: Weight(g17) = 1
    c: Equal(g17,g18)
    c: Equal(g17,g19)
    c: InternalAlignment(g17,g20)
    c: InternalAlignment(g18,g20)
    c: InternalAlignment(g19,g20)
    c: InternalAlignment(g21,g20)
    c: InternalAlignment(g22,g20)
    c: Block(g20)
    c: Block(g23)
    c: Block(g24)
    c: Block(g25)
    c: Block(g26)
    c: Block(g27)
    c: Block(g28)
    c: Coincident(g29,g28)
    c: Coincident(g29,g0)
    c: Block(g13)
    c: Coincident(g31,g30)
    c: Coincident(g31,g28)
    c: Block(g31)
    c: Coincident(g32,g0)
    c: Vertical(g32)
    c: Coincident(g33,g32)
    c: Horizontal(g33)
    c: Coincident(g34,g33)
    c: Vertical(g34)
    c: Block(g33)
    c: Coincident(g35,g13)
    c: Coincident(g35,g34)
    c: Horizontal(g35)
    c: Coincident(g36,g13)
    c: Coincident(g36,g20)
    c: Coincident(g37,g20)
    c: Coincident(g37,g30)
    c: Block(g30)
    c: Coincident(g38,g1)
    c: Coincident(g38,g2)
    c: Coincident(g39,g1)
    c: Coincident(g39,g2)
    c: Coincident(g40,g3)
    c: Coincident(g40,g4)
    c: Coincident(g41,g3)
    c: Coincident(g41,g4)
    c: Coincident(g42,g5)
    c: Coincident(g42,g6)
    c: Coincident(g43,g5)
    c: Coincident(g43,g6)
    c: Coincident(g44,g7)
    c: Coincident(g44,g8)
    c: Coincident(g45,g7)
    c: Coincident(g45,g8)
    c: Distance(g30) = 256
    c: Distance(g33) = 100
FEATURE [Part::Extrusion] Extrude002
  Base = -> Sketch001
  Dir = (1,0,0)
  DirMode = 2
  FaceMakerClass = Part::FaceMakerBullseye
  LengthFwd = 8
  LengthRev = 0
  Solid = true
  Symmetric = false
FEATURE [Sketcher::SketchObject] Sketch002
  FullyConstrained = true
  sketch-geometry (20):
    g0: LineSegment StartX=-2.77179 StartY=-200.304 StartZ=0 EndX=5.22821 EndY=-200.304 EndZ=0
    g1: LineSegment StartX=5.22821 StartY=-200.304 StartZ=0 EndX=5.22821 EndY=-197.304 EndZ=0
    g2: LineSegment StartX=-2.77179 StartY=-200.304 StartZ=0 EndX=-2.77179 EndY=-197.304 EndZ=0
    g3: LineSegment StartX=5.22821 StartY=-197.304 StartZ=0 EndX=8.22821 EndY=-197.304 EndZ=0
    g4: LineSegment StartX=-2.77179 StartY=-197.304 StartZ=0 EndX=-5.77179 EndY=-197.304 EndZ=0
    g5: LineSegment StartX=19.2282 StartY=-203.304 StartZ=0 EndX=19.2282 EndY=-206.304 EndZ=0
    g6: LineSegment StartX=-16.7718 StartY=-203.304 StartZ=0 EndX=-16.7718 EndY=-206.304 EndZ=0
    g7: LineSegment StartX=-16.7718 StartY=-206.304 StartZ=0 EndX=19.2282 EndY=-206.304 EndZ=0
    g8: Circle CenterX=-16.7718 CenterY=-203.304 CenterZ=0 NormalX=0 NormalY=0 NormalZ=1 AngleXU=0 Radius=1
    g9: Circle CenterX=-5.77179 CenterY=-203.304 CenterZ=0 NormalX=0 NormalY=0 NormalZ=1 AngleXU=0 Radius=1
    g10: Circle CenterX=-5.77179 CenterY=-197.304 CenterZ=0 NormalX=0 NormalY=0 NormalZ=1 AngleXU=0 Radius=1
    g11: BSplineCurve PolesCount=3 KnotsCount=2 Degree=2 IsPeriodic=0
    g12: GeomPoint X=-16.7718 Y=-203.304 Z=0
    g13: GeomPoint X=-5.77179 Y=-197.304 Z=0
    g14: Circle CenterX=19.2282 CenterY=-203.304 CenterZ=0 NormalX=0 NormalY=0 NormalZ=1 AngleXU=0 Radius=1
    g15: Circle CenterX=8.22821 CenterY=-203.304 CenterZ=0 NormalX=0 NormalY=0 NormalZ=1 AngleXU=0 Radius=1
    g16: Circle CenterX=8.22821 CenterY=-197.304 CenterZ=0 NormalX=0 NormalY=0 NormalZ=1 AngleXU=0 Radius=1
    g17: BSplineCurve PolesCount=3 KnotsCount=2 Degree=2 IsPeriodic=0
    g18: GeomPoint X=19.2282 Y=-203.304 Z=0
    g19: GeomPoint X=8.22821 Y=-197.304 Z=0
  constraints (41):
    c: Horizontal(g0)
    c: Distance(g0) = 8
    c: Coincident(g1,g0)
    c: Vertical(g1)
    c: Distance(g1) = 3
    c: Coincident(g2,g0)
    c: Vertical(g2)
    c: Distance(g2) = 3
    c: Coincident(g3,g1)
    c: Horizontal(g3)
    c: Distance(g3) = 3
    c: Coincident(g4,g2)
    c: Horizontal(g4)
    c: Distance(g4) = 3
    c: Vertical(g5)
    c: Vertical(g6)
    c: Coincident(g7,g6)
    c: Coincident(g7,g5)
    c: Weight(g8) = 1
    c: Equal(g8,g9)
    c: Equal(g8,g10)
    c: Coincident(g11,g4)
    c: InternalAlignment(g8,g11)
    c: InternalAlignment(g9,g11)
    c: InternalAlignment(g10,g11)
    c: InternalAlignment(g12,g11)
    c: InternalAlignment(g13,g11)
    c: Coincident(g17,g5)
    c: Weight(g14) = 1
    c: Equal(g14,g15)
    c: Equal(g14,g16)
    c: Coincident(g17,g3)
    c: InternalAlignment(g14,g17)
    c: InternalAlignment(g15,g17)
    c: InternalAlignment(g16,g17)
    c: InternalAlignment(g18,g17)
    c: InternalAlignment(g19,g17)
    c: Block(g7)
    c: Block(g17)
    c: Block(g11)
    c: Block(g6)
FEATURE [Part::Extrusion] Extrude003
  Base = -> Sketch002
  Dir = (0,0,1)
  DirMode = 2
  FaceMakerClass = Part::FaceMakerBullseye
  LengthFwd = 260
  LengthRev = 0
  Solid = true
  Symmetric = false
FEATURE [Part::Extrusion] Extrude
  Base = -> Sketch
  Dir = (0,0,1)
  DirMode = 2
  FaceMakerClass = Part::FaceMakerBullseye
  LengthFwd = 14
  LengthRev = 0
  Solid = true
  Symmetric = false
